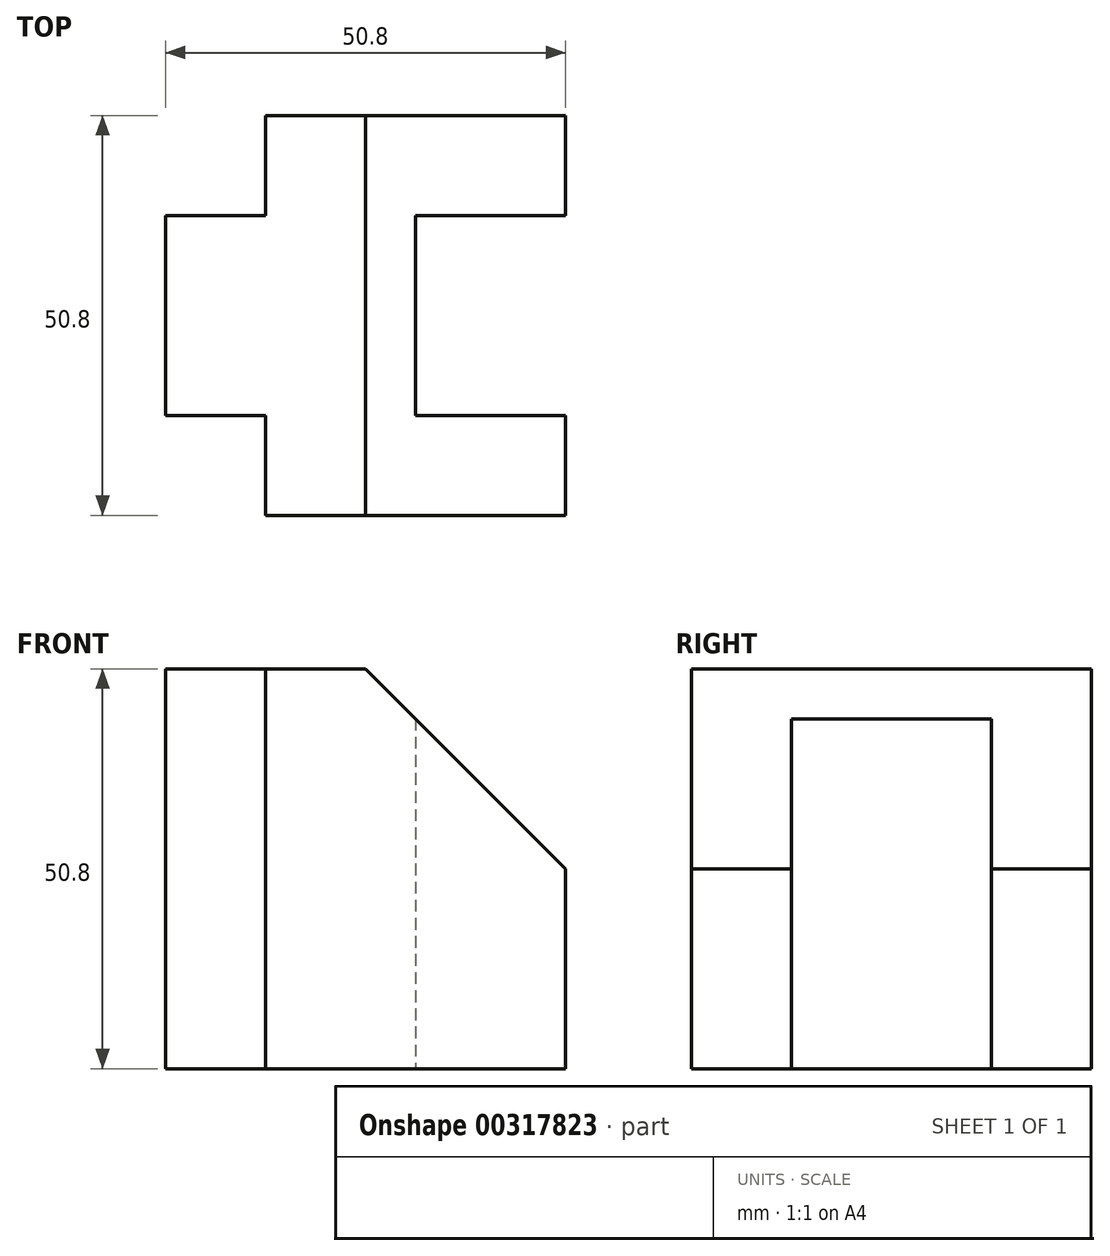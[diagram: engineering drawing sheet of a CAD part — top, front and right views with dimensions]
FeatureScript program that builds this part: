
annotation { "Feature Type Name" : "Feature", "Feature Type Description" : "" }
export const myFeature = defineFeature(function(context is Context, id is Id, definition is map)
    precondition{}
    {
        {
            var Q0;
            Q0=qCreatedBy(makeId("Front.planeOp"),FACE);
            var sketch = newSketch(context, id + "F0", { "sketchPlane" : qUnion([Q0])});
            skLineSegment(sketch, "E0", {"start": v(0, 0) * mm, "end": v(0, 50.8) * mm});
            skLineSegment(sketch, "E1", {"start": v(0, 50.8) * mm, "end": v(12.7, 50.8) * mm});
            skLineSegment(sketch, "E2", {"start": v(12.7, 50.8) * mm, "end": v(12.7, 0) * mm});
            skLineSegment(sketch, "E3", {"start": v(12.7, 0) * mm, "end": v(0, 0) * mm});
            skLineSegment(sketch, "E4", {"start": v(12.7, 50.8) * mm, "end": v(25.4, 50.8) * mm});
            skLineSegment(sketch, "E5", {"start": v(50.8, 0) * mm, "end": v(12.7, 0) * mm});
            skLineSegment(sketch, "E6", {"start": v(25.4, 50.8) * mm, "end": v(50.8, 25.4) * mm});
            skLineSegment(sketch, "E7", {"start": v(50.8, 25.4) * mm, "end": v(50.8, 0) * mm});
            skSolve(sketch);
        }
        {
            var Q0;
            Q0=makeQuery(id+"F0.imprint","IMPRINT",FACE,{"disambiguationData":[TD([[makeQuery(id+"F0.imprint","IMPRINT",EDGE,{"derivedFrom":sQuery(id+"F0.wireOp",EDGE,"E0")}),-1.0]])]});
            extrude(context, id + "F1", {"entities" : qUnion([Q0]), "oppositeDirection" : true, "depth" : 38.1 * mm, "hasSecondDirection" : true, "secondDirectionOppositeDirection" : true, "secondDirectionDepth" : 12.7 * mm});
        }
        {
            var Q0;
            Q0=makeQuery(id+"F0.imprint","IMPRINT",FACE,{"disambiguationData":[TD([[makeQuery(id+"F0.imprint","IMPRINT",EDGE,{"derivedFrom":sQuery(id+"F0.wireOp",EDGE,"E2")}),1.0]])]});
            extrude(context, id + "F2", {"entities" : qUnion([Q0]), "operationType" : NewBodyOperationType.ADD, "oppositeDirection" : true, "depth" : 50.8 * mm});
        }
        {
            var Q0;
            Q0=makeQuery(id+"F2.boolean.opBoolean","MERGE",FACE,{"derivedFrom":[makeQuery(id+"F1.opExtrude","SWEPT_FACE",FACE,{"disambiguationData":[OSD([sQuery(id+"F0.wireOp",EDGE,"E3")])]}),makeQuery(id+"F2.opExtrude","SWEPT_FACE",FACE,{"disambiguationData":[OSD([sQuery(id+"F0.wireOp",EDGE,"E5")])]})]});
            var sketch = newSketch(context, id + "F3", { "sketchPlane" : qUnion([Q0])});
            skLineSegment(sketch, "E8", {"start": v(50.8, 0) * mm, "end": v(25.4, 0) * mm});
            skLineSegment(sketch, "E9", {"start": v(25.4, 0) * mm, "end": v(25.4, -50.8) * mm});
            skLineSegment(sketch, "E10", {"start": v(25.4, -50.8) * mm, "end": v(50.8, -50.8) * mm});
            skLineSegment(sketch, "E11", {"start": v(50.8, -50.8) * mm, "end": v(50.8, -38.1) * mm});
            skLineSegment(sketch, "E12", {"start": v(50.8, -38.1) * mm, "end": v(31.75, -38.1) * mm});
            skLineSegment(sketch, "E13", {"start": v(31.75, -38.1) * mm, "end": v(31.75, -12.7) * mm});
            skLineSegment(sketch, "E14", {"start": v(31.75, -12.7) * mm, "end": v(50.8, -12.7) * mm});
            skLineSegment(sketch, "E15", {"start": v(50.8, -12.7) * mm, "end": v(50.8, 0) * mm});
            skSolve(sketch);
        }
        {
            var Q0;
            {var subQ0=sQuery(id+"F3.wireOp",EDGE,"E12");Q0=makeQuery(id+"F3.imprint","IMPRINT",FACE,{"disambiguationData":[TD([[makeQuery(id+"F3.imprint","IMPRINT",EDGE,{"derivedFrom":subQ0}),-1.0]])]});}
            extrude(context, id + "F4", {"entities" : qUnion([Q0]), "operationType" : NewBodyOperationType.REMOVE, "oppositeDirection" : true, "depth" : 50.8 * mm});
        }
    });
